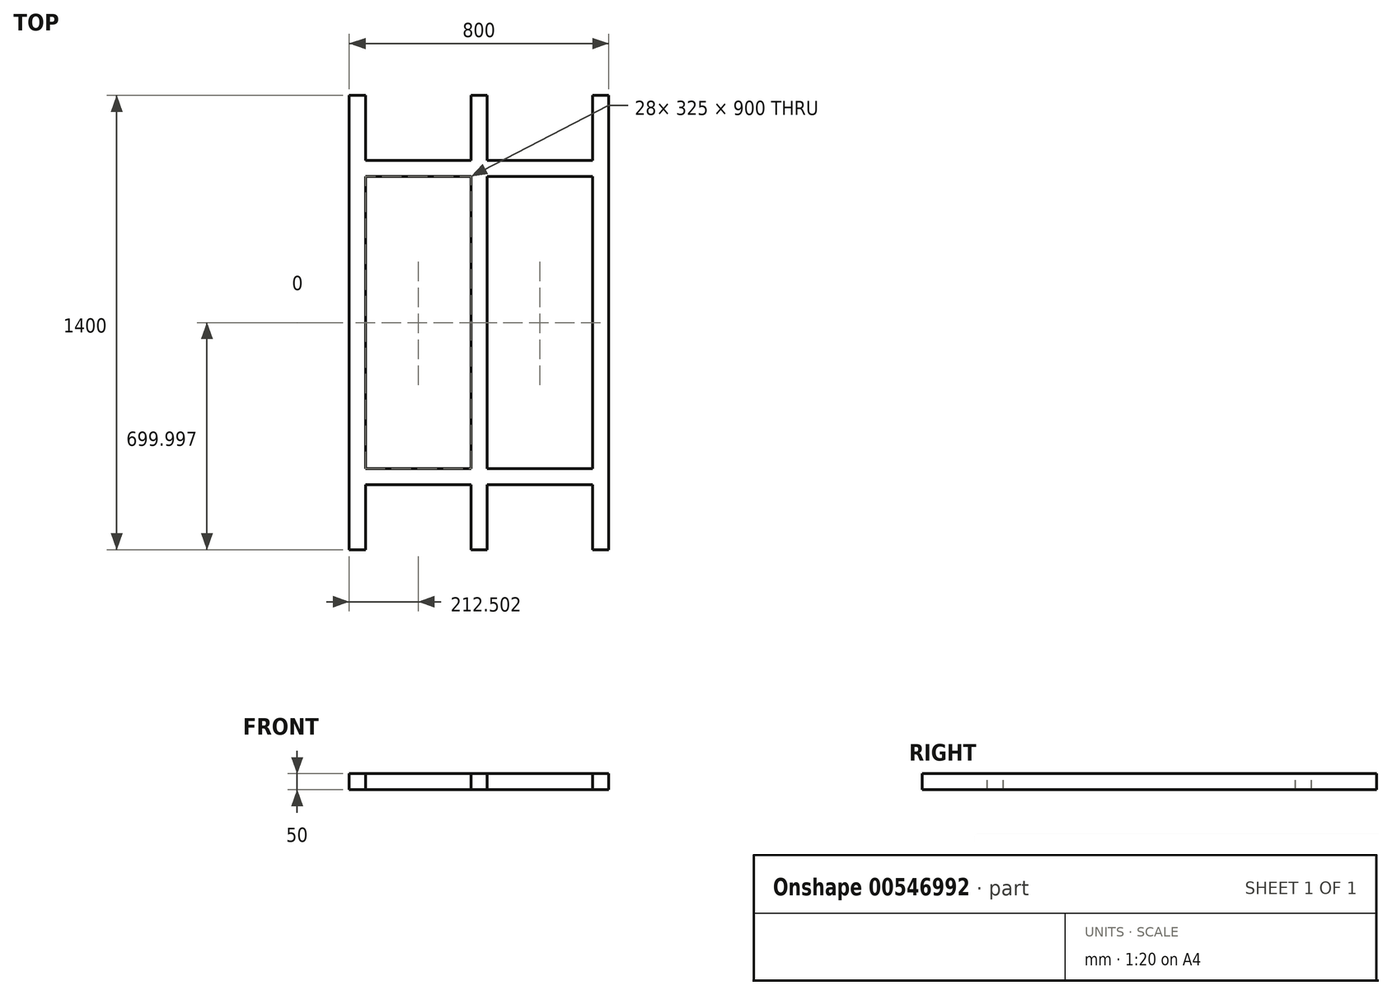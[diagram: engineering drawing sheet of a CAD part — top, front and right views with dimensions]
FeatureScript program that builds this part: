
annotation { "Feature Type Name" : "Feature", "Feature Type Description" : "" }
export const myFeature = defineFeature(function(context is Context, id is Id, definition is map)
    precondition{}
    {
        {
            var Q0;
            Q0=qCreatedBy(makeId("Top.planeOp"),FACE);
            var sketch = newSketch(context, id + "F0", { "sketchPlane" : qUnion([Q0])});
            skLineSegment(sketch, "E0.bottom", {"start": v(-143.73, 1272.15) * mm, "end": v(656.27, 1272.15) * mm});
            skLineSegment(sketch, "E0.top", {"start": v(-143.73, -127.85) * mm, "end": v(656.27, -127.85) * mm});
            skLineSegment(sketch, "E0.left", {"start": v(-143.73, 1272.15) * mm, "end": v(-143.73, -127.85) * mm});
            skLineSegment(sketch, "E0.right", {"start": v(656.27, 1272.15) * mm, "end": v(656.27, -127.85) * mm});
            skSolve(sketch);
        }
        {
            var Q0;
            Q0 = qSketchRegion(id + "F0", true);
            extrude(context, id + "F1", {"entities" : qUnion([Q0]), "depth" : 50 * mm, "offsetDistance" : 25 * mm});
        }
        {
            var Q0;
            Q0=makeQuery(id+"F1.opExtrude","CAP_FACE",FACE,{"disambiguationData":[OSD([sQuery(id+"F0.wireOp",EDGE,"E0.bottom"),sQuery(id+"F0.wireOp",EDGE,"E0.top"),sQuery(id+"F0.wireOp",EDGE,"E0.left"),sQuery(id+"F0.wireOp",EDGE,"E0.right")])],"isStart":false});
            var sketch = newSketch(context, id + "F2", { "sketchPlane" : qUnion([Q0])});
            skLineSegment(sketch, "E1.bottom", {"start": v(-93.73, 1272.15) * mm, "end": v(231.27, 1272.15) * mm});
            skLineSegment(sketch, "E1.top", {"start": v(-93.73, 1072.15) * mm, "end": v(231.27, 1072.15) * mm});
            skLineSegment(sketch, "E1.left", {"start": v(-93.73, 1272.15) * mm, "end": v(-93.73, 1072.15) * mm});
            skLineSegment(sketch, "E1.right", {"start": v(231.27, 1272.15) * mm, "end": v(231.27, 1072.15) * mm});
            skLineSegment(sketch, "E2.bottom", {"start": v(231.27, -127.85) * mm, "end": v(-93.73, -127.85) * mm});
            skLineSegment(sketch, "E2.top", {"start": v(231.27, 72.15) * mm, "end": v(-93.73, 72.15) * mm});
            skLineSegment(sketch, "E2.left", {"start": v(231.27, -127.85) * mm, "end": v(231.27, 72.15) * mm});
            skLineSegment(sketch, "E2.right", {"start": v(-93.73, -127.85) * mm, "end": v(-93.73, 72.15) * mm});
            skLineSegment(sketch, "E3.bottom", {"start": v(-93.73, 1022.15) * mm, "end": v(231.27, 1022.15) * mm});
            skLineSegment(sketch, "E3.top", {"start": v(-93.73, 122.15) * mm, "end": v(231.27, 122.15) * mm});
            skLineSegment(sketch, "E3.left", {"start": v(-93.73, 1022.15) * mm, "end": v(-93.73, 122.15) * mm});
            skLineSegment(sketch, "E3.right", {"start": v(231.27, 1022.15) * mm, "end": v(231.27, 122.15) * mm});
            skLineSegment(sketch, "E4.bottom", {"start": v(606.27, 1272.15) * mm, "end": v(281.27, 1272.15) * mm});
            skLineSegment(sketch, "E4.top", {"start": v(606.27, 1072.15) * mm, "end": v(281.27, 1072.15) * mm});
            skLineSegment(sketch, "E4.left", {"start": v(606.27, 1272.15) * mm, "end": v(606.27, 1072.15) * mm});
            skLineSegment(sketch, "E4.right", {"start": v(281.27, 1272.15) * mm, "end": v(281.27, 1072.15) * mm});
            skLineSegment(sketch, "E5.bottom", {"start": v(281.27, 1022.15) * mm, "end": v(606.27, 1022.15) * mm});
            skLineSegment(sketch, "E5.top", {"start": v(281.27, 122.15) * mm, "end": v(606.27, 122.15) * mm});
            skLineSegment(sketch, "E5.left", {"start": v(281.27, 1022.15) * mm, "end": v(281.27, 122.15) * mm});
            skLineSegment(sketch, "E5.right", {"start": v(606.27, 1022.15) * mm, "end": v(606.27, 122.15) * mm});
            skLineSegment(sketch, "E6.bottom", {"start": v(606.27, 72.15) * mm, "end": v(281.27, 72.15) * mm});
            skLineSegment(sketch, "E6.top", {"start": v(606.27, -127.85) * mm, "end": v(281.27, -127.85) * mm});
            skLineSegment(sketch, "E6.left", {"start": v(606.27, 72.15) * mm, "end": v(606.27, -127.85) * mm});
            skLineSegment(sketch, "E6.right", {"start": v(281.27, 72.15) * mm, "end": v(281.27, -127.85) * mm});
            skSolve(sketch);
        }
        {
            var Q0;
            Q0 = qSketchRegion(id + "F2", true);
            extrude(context, id + "F3", {"entities" : qUnion([Q0]), "operationType" : NewBodyOperationType.REMOVE, "oppositeDirection" : true, "depth" : 50 * mm, "offsetDistance" : 25 * mm});
        }
    });
